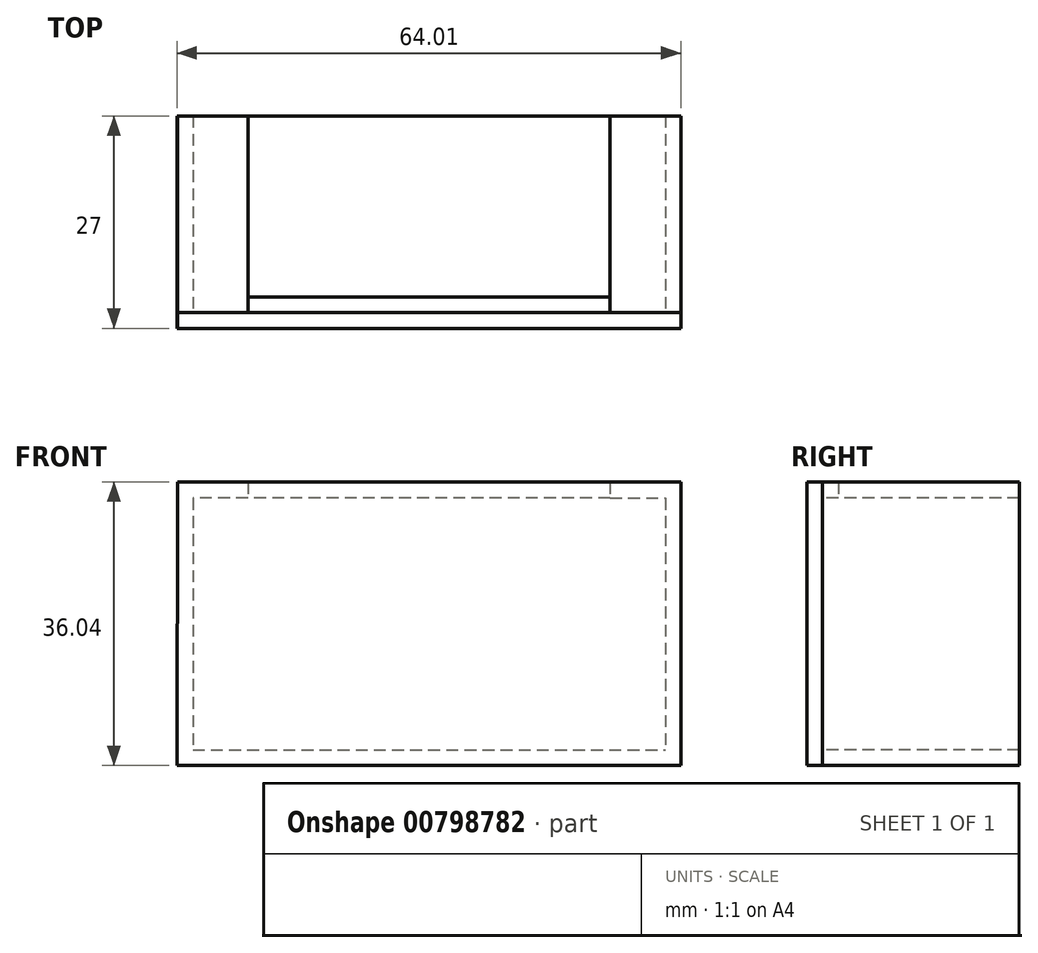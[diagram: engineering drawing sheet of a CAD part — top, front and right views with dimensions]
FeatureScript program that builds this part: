
annotation { "Feature Type Name" : "Feature", "Feature Type Description" : "" }
export const myFeature = defineFeature(function(context is Context, id is Id, definition is map)
    precondition{}
    {
        {
            var Q0;
            Q0=qCreatedBy(makeId("Front.planeOp"),FACE);
            var sketch = newSketch(context, id + "F0", { "sketchPlane" : qUnion([Q0])});
            skLineSegment(sketch, "E0", {"start": v(0, 25.63) * mm, "end": v(60, 25.63) * mm});
            skLineSegment(sketch, "E1", {"start": v(61.98, 23.63) * mm, "end": v(-2.03, 23.63) * mm});
            skLineSegment(sketch, "E2", {"start": v(53, 59.67) * mm, "end": v(53, 57.63) * mm});
            skLineSegment(sketch, "E3", {"start": v(53, 57.63) * mm, "end": v(60, 57.63) * mm});
            skLineSegment(sketch, "E4", {"start": v(-1.96, 59.63) * mm, "end": v(7, 59.63) * mm});
            skLineSegment(sketch, "E5", {"start": v(7, 59.63) * mm, "end": v(7, 57.63) * mm});
            skLineSegment(sketch, "E6", {"start": v(7, 57.63) * mm, "end": v(0, 57.63) * mm});
            skLineSegment(sketch, "E7", {"start": v(53, 59.67) * mm, "end": v(61.98, 59.67) * mm});
            skLineSegment(sketch, "E8", {"start": v(0, 57.63) * mm, "end": v(0, 25.63) * mm});
            skLineSegment(sketch, "E9", {"start": v(-1.96, 59.63) * mm, "end": v(-2.03, 23.63) * mm});
            skLineSegment(sketch, "E10", {"start": v(60, 57.63) * mm, "end": v(60, 25.63) * mm});
            skLineSegment(sketch, "E11", {"start": v(61.98, 59.67) * mm, "end": v(61.98, 23.63) * mm});
            skLineSegment(sketch, "E12", {"start": v(-1.96, 59.63) * mm, "end": v(61.98, 59.67) * mm});
            skLineSegment(sketch, "E13", {"start": v(-1.96, 57.75) * mm, "end": v(-1.96, 59.63) * mm});
            skLineSegment(sketch, "E14", {"start": v(53, 57.63) * mm, "end": v(7, 57.63) * mm});
            skLineSegment(sketch, "E15", {"start": v(53, 59.67) * mm, "end": v(7, 59.63) * mm});
            skSolve(sketch);
        }
        {
            var Q0;
            {var subQ6=sQuery(id+"F0.wireOp",EDGE,"E5");Q0=makeQuery(id+"F0.imprint","IMPRINT",FACE,{"disambiguationData":[TD([[makeQuery(id+"F0.imprint","IMPRINT",EDGE,{"derivedFrom":subQ6}),1.0]])]});}
            extrude(context, id + "F1", {"entities" : qUnion([Q0]), "oppositeDirection" : true, "depth" : 2 * mm, "offsetDistance" : 25 * mm});
        }
        {
            var Q0;
            Q0=makeQuery(id+"F0.imprint","IMPRINT",FACE,{"disambiguationData":[TD([[makeQuery(id+"F0.imprint","IMPRINT",EDGE,{"derivedFrom":sQuery(id+"F0.wireOp",EDGE,"E0")}),-1.0]])]});
            var Q1;
            {var subQ6=sQuery(id+"F0.wireOp",EDGE,"E5");Q1=makeQuery(id+"F0.imprint","IMPRINT",FACE,{"disambiguationData":[TD([[makeQuery(id+"F0.imprint","IMPRINT",EDGE,{"derivedFrom":subQ6}),1.0]])]});}
            var Q2;
            Q2=makeQuery(id+"F0.imprint","IMPRINT",FACE,{"disambiguationData":[TD([[makeQuery(id+"F0.imprint","IMPRINT",EDGE,{"derivedFrom":sQuery(id+"F0.wireOp",EDGE,"E0")}),1.0]])]});
            extrude(context, id + "F2", {"entities" : qUnion([Q0, Q1, Q2]), "depth" : 2 * mm, "offsetDistance" : 25 * mm});
        }
        {
            var Q0;
            Q0=makeQuery(id+"F0.imprint","IMPRINT",FACE,{"disambiguationData":[TD([[makeQuery(id+"F0.imprint","IMPRINT",EDGE,{"derivedFrom":sQuery(id+"F0.wireOp",EDGE,"E0")}),-1.0]])]});
            extrude(context, id + "F3", {"entities" : qUnion([Q0]), "oppositeDirection" : true, "depth" : 25 * mm, "offsetDistance" : 25 * mm});
        }
    });
